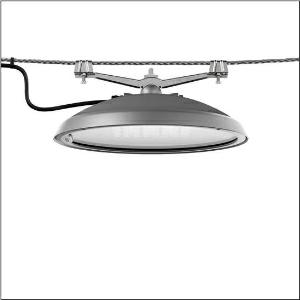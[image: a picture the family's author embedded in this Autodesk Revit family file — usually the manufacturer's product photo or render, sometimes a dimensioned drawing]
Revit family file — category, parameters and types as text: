
# Revit family: dl_r__50_iq_mini___st1_0s_5xa248w31f08ge_208e
name_source: partatom
category: Lighting Fixtures
units: mm (PartAtom-declared; Revit-internal decimal feet)

## family parameters
Cut with Voids When Loaded = No
Host = Face
Light Source = No
Part Type = Normal
Room Calculation Point = No
Round Connector Dimension = Use Diameter
Shared = No

## types (1)
- --- (1 x LED, 5190 lm, 32.7 W, 3000K)
    Apparent Load = 33 VA
    CIE Flux Codes = 37 72 97 100 100
    Color Rendering = 70
    Color Temperature = 3000K
    Default Elevation = 1800 mm
    Description = DL® 50 iQ mini, catenary luminaire, primary light control with lens, of PMMA, primary optical cover: cover, of toughened safety glass, transparent, light distribution: ST1.0s, light emission: direct distribution, primary light characteristic: symmetric, installation type: suspended mounting, LED, High Power LED, rated luminous flux: 5.190lm, luminous efficacy: 159lm/W, light colour: 730, colour temperature: 3000K, control: optimised constant luminous flux control (CLO 2.0), Desk-Remote (wireless, voltage-free reading and setting of iQ features in the workshop via application-optimized NFC function/RFID function), Light-Fading, Smart-Wire, Night-Set, Lumen-Switch, Temp-Guard, Auto-Match, Street-Remote, mains connection: 230..240V, AC, 50/60Hz, start of lifetime: 33W, end of service life: 34W, reduction: 16W, luminaire housing, of diecast aluminium, powder-coated, Siteco® metallic grey (DB 702S), diameter: 500mm, height: 115mm, protection rating (complete): IP66, insulation class (complete): insulation class II (safety insulation), certification: CE, ENEC, VDE, impact resistance: IK08, permissible operating ambient temperature for outdoor applications: -25..+40°C, standard-compliant lighting for roads and squares, packaging unit: 1 piece

Light Distribution: ST1.0s
    Height = 124 mm  [stored 0.406824 ft]
    Lamp = 1 x LED
    Lamp Light Flux = 5190 lm
    Lamp Power = 32.7 W
    Lamp count = 1
    Length = 500 mm
    Luminous efficacy = 159 lm/W
    Manufacturer = Siteco
    ModVariant = No
    Model = 5XA248W31F08GE
    Number of Poles = 1
    OnlyDefault = Yes
    Power Factor = 1
    Product Name = DL® 50 iQ mini | ST1.0s
    Product group = catenary luminaire
    ProductGroupID = 6300
    Protection Class = Protection class II
    Protection Degree = IP 66
    RLX_Detail_Level = 1
    RLX_Emergency_Light_Flux = 0 lm
    RLX_Emergency_Type = 0
    RLX_Emergency_Type_DB = No
    RlxData = <blob elided: 123969 chars, md5=cd52e793>
    Socket = socket
    Standby Power = 0 W
    System Light Flux = 5190 lm
    System Power = 33 W
    Type Comments = factory setting: luminous flux: 100 % | dim-lin: 254 | 340 mA
    Type Image = l_1242791.jpg
    URL = http://relux.com
    VarID = @adj_072193
    Voltage = 0 V
    Weight = 0.00 kg
    Width = 0 mm  [stored 0 ft]

note: [stored X ft] marks values corroborated as IEEE doubles in the binary element streams (Revit-internal decimal feet)

## geometry (parser evidence)
native form markers: Blend x4, Sweep x13
no freeform markers — native parametric forms only
